# Revit family: DAL_A3-Bifold-2700x3990-BF2740R4
name_source: partatom
category: Doors
revit_build: Autodesk Revit 2016 (Build: 20150220_1215(x64)
units: mm (PartAtom-declared; Revit-internal decimal feet)

## family parameters
Always vertical = Yes
Cut with Voids When Loaded = No
Host = Wall
Room Calculation Point = No
Shared = No

## types (1)
- 2700 x 3990 BF2740R4
    Assembly Code = B2030130
    Frame Depth = 20 mm  [stored 0.0656168 ft]
    Frame Material = Wood - Meranti
    Function = Interior
    Glass Material = Glass
    Height = 2700 mm  [stored 8.85827 ft]
    Manufacturer = Canterbury Windows & Doors
    Manufacturer Code = BF2740R4
    Model = Standard Bifold Door
    Opening Angle = 80.00°
    Opening Angle 2 = 160.00°
    Panel Material = Wood - Meranti
    Panel Width = 973 mm
    Rough Height = 2720 mm  [stored 8.92388 ft]
    Rough Width = 4010 mm
    URL = http://www.canterburywindows.com.au
    Wall Closure = By host
    Width = 3990 mm  [stored 13.0906 ft]

note: [stored X ft] marks values corroborated as IEEE doubles in the binary element streams (Revit-internal decimal feet)

## geometry (parser evidence)
native form markers: Sweep x1
no freeform markers — native parametric forms only
